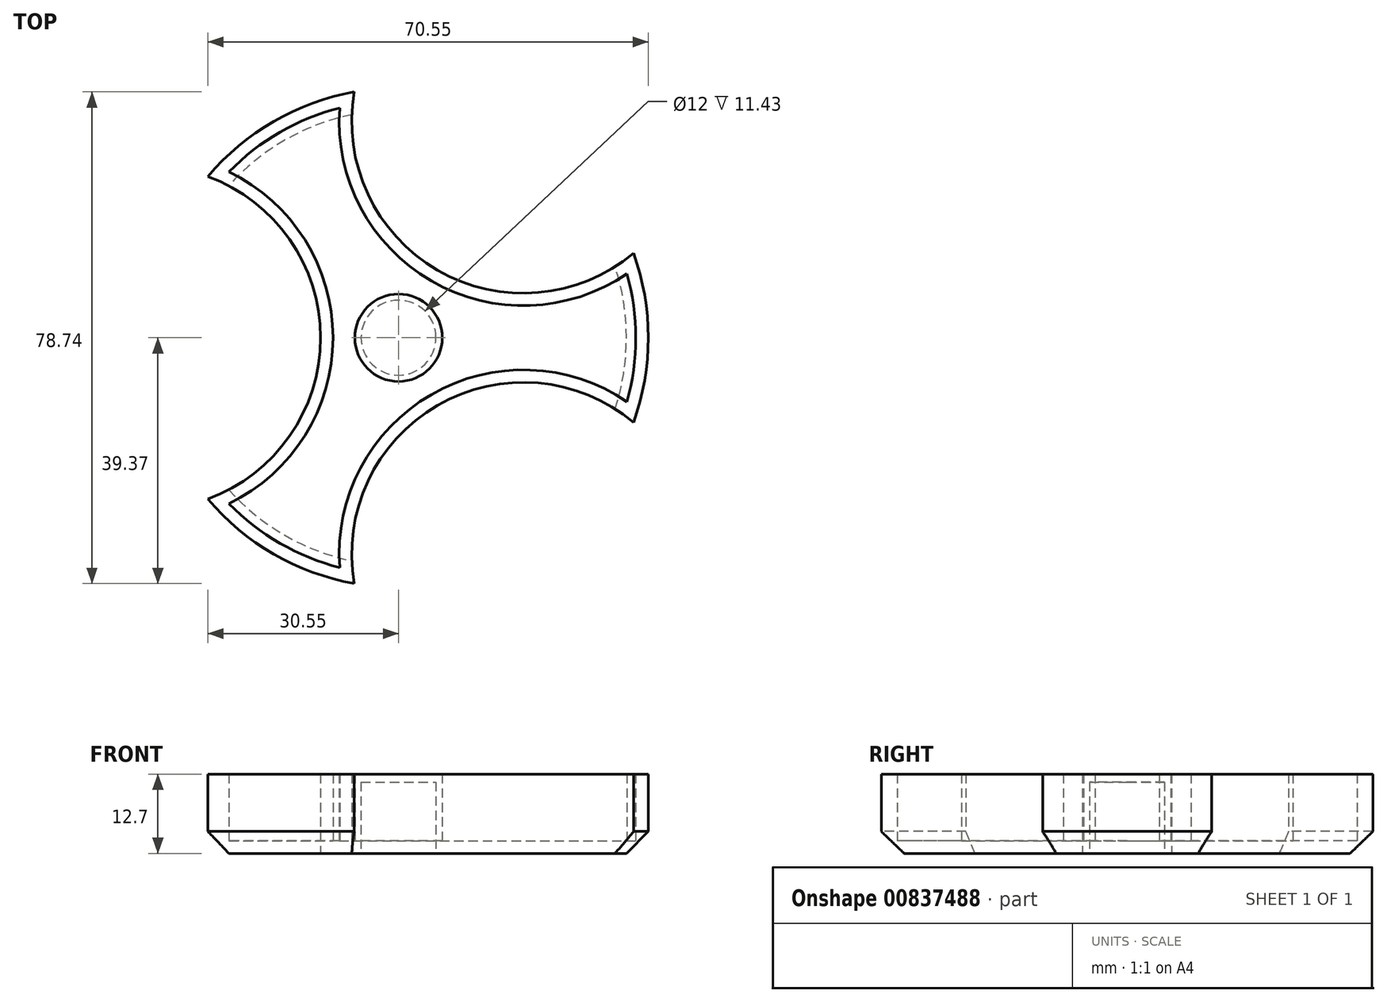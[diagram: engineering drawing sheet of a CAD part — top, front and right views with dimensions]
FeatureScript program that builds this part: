
annotation { "Feature Type Name" : "Feature", "Feature Type Description" : "" }
export const myFeature = defineFeature(function(context is Context, id is Id, definition is map)
    precondition{}
    {
        {
            var Q0;
            Q0=qCreatedBy(makeId("Top.planeOp"),FACE);
            var sketch = newSketch(context, id + "F0", { "sketchPlane" : qUnion([Q0])});
            skArc(sketch, "E0", {"start": v(-7.1, 39.37) * mm, "mid": v(-20, 34.64) * mm, "end": v(-30.55, 25.82) * mm});
            skArc(sketch, "E1", {"start": v(-30.55, -25.82) * mm, "mid": v(-12.5, 0) * mm, "end": v(-30.55, 25.82) * mm});
            skArc(sketch, "E2.1.0", {"start": v(37.64, -13.54) * mm, "mid": v(6.25, -10.83) * mm, "end": v(-7.1, -39.37) * mm});
            skArc(sketch, "E2.2.0", {"start": v(-7.1, 39.37) * mm, "mid": v(6.25, 10.83) * mm, "end": v(37.64, 13.54) * mm});
            skArc(sketch, "E3.trimOffspring", {"start": v(37.64, -13.54) * mm, "mid": v(40, 0) * mm, "end": v(37.64, 13.54) * mm});
            skArc(sketch, "E4.trimOffspring", {"start": v(-30.55, -25.82) * mm, "mid": v(-20, -34.64) * mm, "end": v(-7.1, -39.37) * mm});
            skSolve(sketch);
        }
        {
            var Q0;
            Q0 = qSketchRegion(id + "F0", true);
            extrude(context, id + "F1", {"entities" : qUnion([Q0]), "depth" : 12.7 * mm, "offsetDistance" : 25 * mm});
        }
        {
            var Q0;
            Q0=makeQuery(id+"F1.opExtrude","CAP_FACE",FACE,{"disambiguationData":[OSD([sQuery(id+"F0.wireOp",EDGE,"E0")])],"isStart":false});
            shell(context, id + "F2", {"entities" : qUnion([Q0]), "thickness" : 2 * mm});
        }
        {
            var Q0;
            Q0=makeQuery(id+"F1.opExtrude","CAP_FACE",FACE,{"disambiguationData":[OSD([sQuery(id+"F0.wireOp",EDGE,"E0"),sQuery(id+"F0.wireOp",EDGE,"E1"),sQuery(id+"F0.wireOp",EDGE,"E2.1.0"),sQuery(id+"F0.wireOp",EDGE,"E2.2.0"),sQuery(id+"F0.wireOp",EDGE,"E3.trimOffspring"),sQuery(id+"F0.wireOp",EDGE,"E4.trimOffspring")])],"isStart":true});
            var sketch = newSketch(context, id + "F3", { "sketchPlane" : qUnion([Q0])});
            skCircle(sketch, "E5", {"center": v(0, 0) * mm, "radius": 7 * mm});
            skSolve(sketch);
        }
        {
            var Q0;
            Q0 = qSketchRegion(id + "F3", true);
            extrude(context, id + "F4", {"entities" : qUnion([Q0]), "operationType" : NewBodyOperationType.ADD, "oppositeDirection" : true, "depth" : 12.7 * mm, "offsetDistance" : 25 * mm});
        }
        {
            var Q0;
            Q0=makeQuery(id+"F1.opExtrude","CAP_FACE",FACE,{"disambiguationData":[OSD([sQuery(id+"F0.wireOp",EDGE,"E0"),sQuery(id+"F0.wireOp",EDGE,"E1"),sQuery(id+"F0.wireOp",EDGE,"E2.1.0"),sQuery(id+"F0.wireOp",EDGE,"E2.2.0"),sQuery(id+"F0.wireOp",EDGE,"E3.trimOffspring"),sQuery(id+"F0.wireOp",EDGE,"E4.trimOffspring")])],"isStart":true});
            var sketch = newSketch(context, id + "F5", { "sketchPlane" : qUnion([Q0])});
            skCircle(sketch, "E6", {"center": v(0, 0) * mm, "radius": 6 * mm});
            skSolve(sketch);
        }
        {
            var Q0;
            Q0=makeQuery(id+"F5.imprint","IMPRINT",FACE,{"disambiguationData":[TD([[makeQuery(id+"F5.imprint","IMPRINT",EDGE,{"derivedFrom":sQuery(id+"F5.wireOp",EDGE,"E6")}),1.0]])]});
            extrude(context, id + "F6", {"entities" : qUnion([Q0]), "operationType" : NewBodyOperationType.REMOVE, "oppositeDirection" : true, "depth" : 11.43 * mm, "offsetDistance" : 25 * mm});
        }
        {
            var Q0;
            Q0=makeQuery(id+"F1.opExtrude","CAP_EDGE",EDGE,{"disambiguationData":[OSD([sQuery(id+"F0.wireOp",EDGE,"E3.trimOffspring")])],"isStart":true});
            var Q1;
            Q1=makeQuery(id+"F1.opExtrude","CAP_EDGE",EDGE,{"disambiguationData":[OSD([sQuery(id+"F0.wireOp",EDGE,"E4.trimOffspring")])],"isStart":true});
            var Q2;
            Q2=makeQuery(id+"F1.opExtrude","CAP_EDGE",EDGE,{"disambiguationData":[OSD([sQuery(id+"F0.wireOp",EDGE,"E0")])],"isStart":true});
            chamfer(context, id + "F7", {"entities" : qUnion([Q0, Q1, Q2]), "width" : 3.5 * mm, "tangentPropagation" : true});
        }
    });
